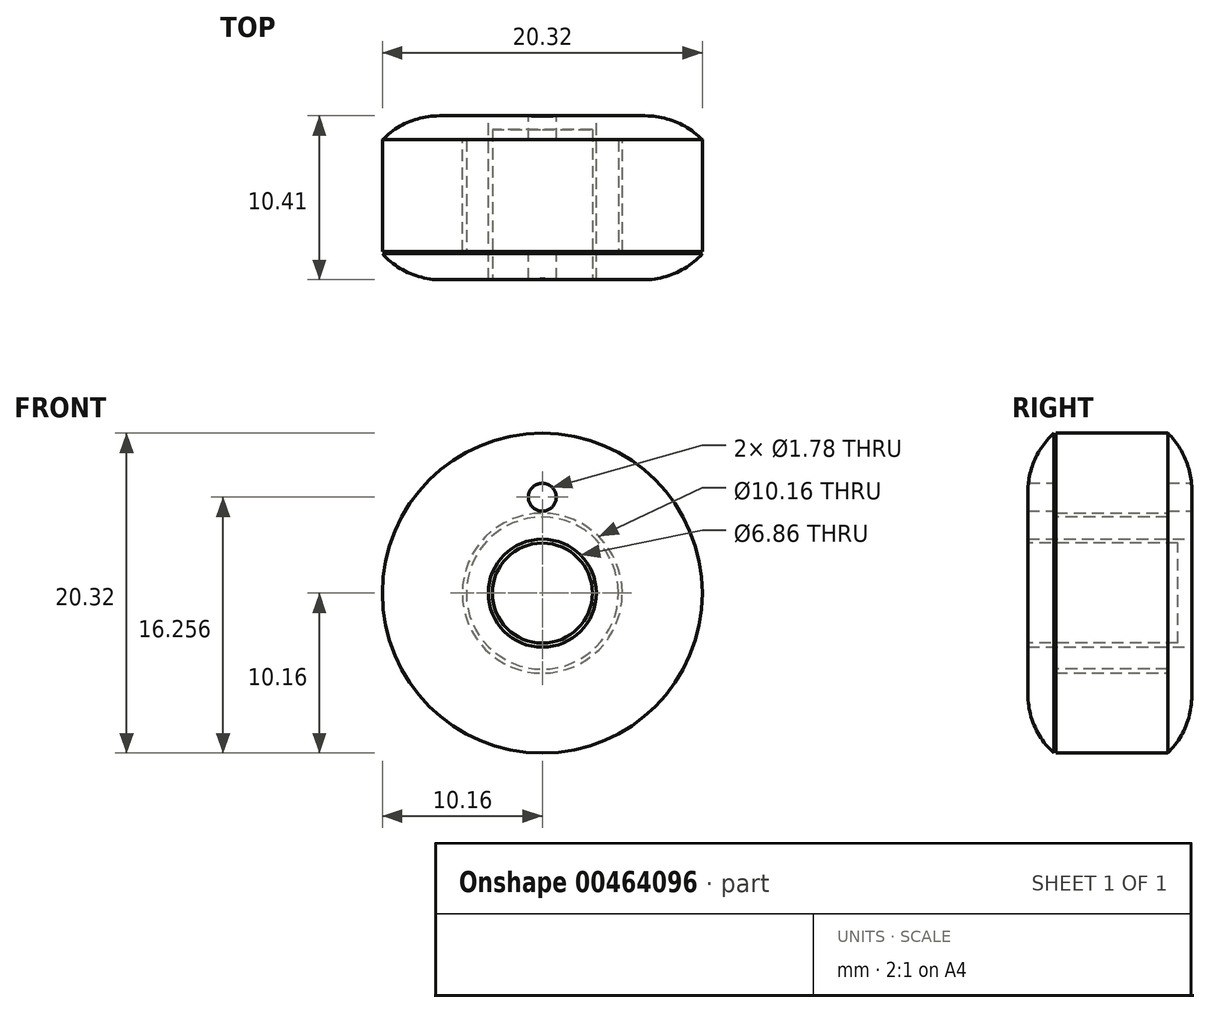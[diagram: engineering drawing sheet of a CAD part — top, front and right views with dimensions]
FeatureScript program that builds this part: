
annotation { "Feature Type Name" : "Feature", "Feature Type Description" : "" }
export const myFeature = defineFeature(function(context is Context, id is Id, definition is map)
    precondition{}
    {
        {
            var Q0;
            Q0=qCreatedBy(makeId("Front.planeOp"),FACE);
            var sketch = newSketch(context, id + "F0", { "sketchPlane" : qUnion([Q0])});
            skCircle(sketch, "E0", {"center": v(0, 0) * mm, "radius": 10.16 * mm});
            skCircle(sketch, "E1", {"center": v(0, 0) * mm, "radius": 3.43 * mm});
            skSolve(sketch);
        }
        {
            var Q0;
            Q0 = qSketchRegion(id + "F0", true);
            extrude(context, id + "F1", {"entities" : qUnion([Q0]), "depth" : 10.4 * mm});
        }
        {
            var Q0;
            Q0=qCreatedBy(makeId("Right.planeOp"),FACE);
            var sketch = newSketch(context, id + "F2", { "sketchPlane" : qUnion([Q0])});
            skLineSegment(sketch, "E2.bottom", {"start": v(-8.76, 10.41) * mm, "end": v(-1.52, 10.41) * mm});
            skLineSegment(sketch, "E2.top", {"start": v(-8.76, 4.83) * mm, "end": v(-1.52, 4.83) * mm});
            skLineSegment(sketch, "E2.left", {"start": v(-8.76, 10.41) * mm, "end": v(-8.76, 4.83) * mm});
            skLineSegment(sketch, "E2.right", {"start": v(-1.52, 10.41) * mm, "end": v(-1.52, 4.83) * mm});
            skLineSegment(sketch, "E3", {"start": v(-5.17, -10.06) * mm, "end": v(-5.17, 2.31) * mm});
            skSolve(sketch);
        }
        {
            var Q0;
            Q0 = qSketchRegion(id + "F2", true);
            var Q1;
            Q1=makeQuery(id+"F1.opExtrude","CAP_EDGE",EDGE,{"disambiguationData":[OSD([sQuery(id+"F0.wireOp",EDGE,"E1")])],"isStart":false});
            revolve(context, id + "F3", {"operationType" : NewBodyOperationType.REMOVE, "entities" : qUnion([Q0]), "axis" : qUnion([Q1]), "revolveType" : RevolveType.FULL, "oppositeDirection" : true});
        }
        {
            var Q0;
            Q0=makeQuery(id+"F1.opExtrude","CAP_FACE",FACE,{"disambiguationData":[OSD([sQuery(id+"F0.wireOp",EDGE,"E0"),sQuery(id+"F0.wireOp",EDGE,"E1")])],"isStart":true});
            var sketch = newSketch(context, id + "F4", { "sketchPlane" : qUnion([Q0])});
            skCircle(sketch, "E4", {"center": v(0, 6.1) * mm, "radius": 0.89 * mm});
            skSolve(sketch);
        }
        {
            var Q0;
            Q0 = qSketchRegion(id + "F4", true);
            extrude(context, id + "F5", {"entities" : qUnion([Q0]), "operationType" : NewBodyOperationType.REMOVE, "endBound" : BoundingType.THROUGH_ALL, "oppositeDirection" : true, "depth" : 25.4 * mm});
        }
        {
            var Q0;
            Q0=qCreatedBy(makeId("Right.planeOp"),FACE);
            var sketch = newSketch(context, id + "F6", { "sketchPlane" : qUnion([Q0])});
            skLineSegment(sketch, "E5.bottom", {"start": v(-8.64, 5.08) * mm, "end": v(-1.52, 5.08) * mm});
            skLineSegment(sketch, "E5.top", {"start": v(-8.64, 10.16) * mm, "end": v(-1.52, 10.16) * mm});
            skLineSegment(sketch, "E5.left", {"start": v(-8.64, 5.08) * mm, "end": v(-8.64, 10.16) * mm});
            skLineSegment(sketch, "E5.right", {"start": v(-1.52, 5.08) * mm, "end": v(-1.52, 10.16) * mm});
            skSolve(sketch);
        }
        {
            var Q0;
            Q0 = qSketchRegion(id + "F6", true);
            var Q1;
            Q1=makeQuery(id+"F1.opExtrude","CAP_EDGE",EDGE,{"disambiguationData":[OSD([sQuery(id+"F0.wireOp",EDGE,"E0")])],"isStart":false});
            revolve(context, id + "F7", {"entities" : qUnion([Q0]), "axis" : qUnion([Q1]), "revolveType" : RevolveType.FULL});
        }
        {
            var Q0;
            Q0=makeQuery(id+"F1.opExtrude","CAP_FACE",FACE,{"disambiguationData":[OSD([sQuery(id+"F0.wireOp",EDGE,"E0"),sQuery(id+"F0.wireOp",EDGE,"E1")])],"isStart":false});
            var sketch = newSketch(context, id + "F8", { "sketchPlane" : qUnion([Q0])});
            skCircle(sketch, "E6", {"center": v(0, 0) * mm, "radius": 3.18 * mm});
            skSolve(sketch);
        }
        {
            var Q0;
            Q0 = qSketchRegion(id + "F8", true);
            extrude(context, id + "F9", {"entities" : qUnion([Q0]), "oppositeDirection" : true, "depth" : 9.52 * mm});
        }
        {
            var Q0;
            Q0=makeQuery(id+"F1.opExtrude","CAP_EDGE",EDGE,{"disambiguationData":[OSD([sQuery(id+"F0.wireOp",EDGE,"E0")])],"isStart":false});
            var Q1;
            Q1=makeQuery(id+"F1.opExtrude","CAP_EDGE",EDGE,{"disambiguationData":[OSD([sQuery(id+"F0.wireOp",EDGE,"E0")])],"isStart":true});
            fillet(context, id + "F10", {"entities" : qUnion([Q0, Q1]), "radius" : 5.08 * mm, "tangentPropagation" : true, "allowEdgeOverflow" : false});
        }
    });
